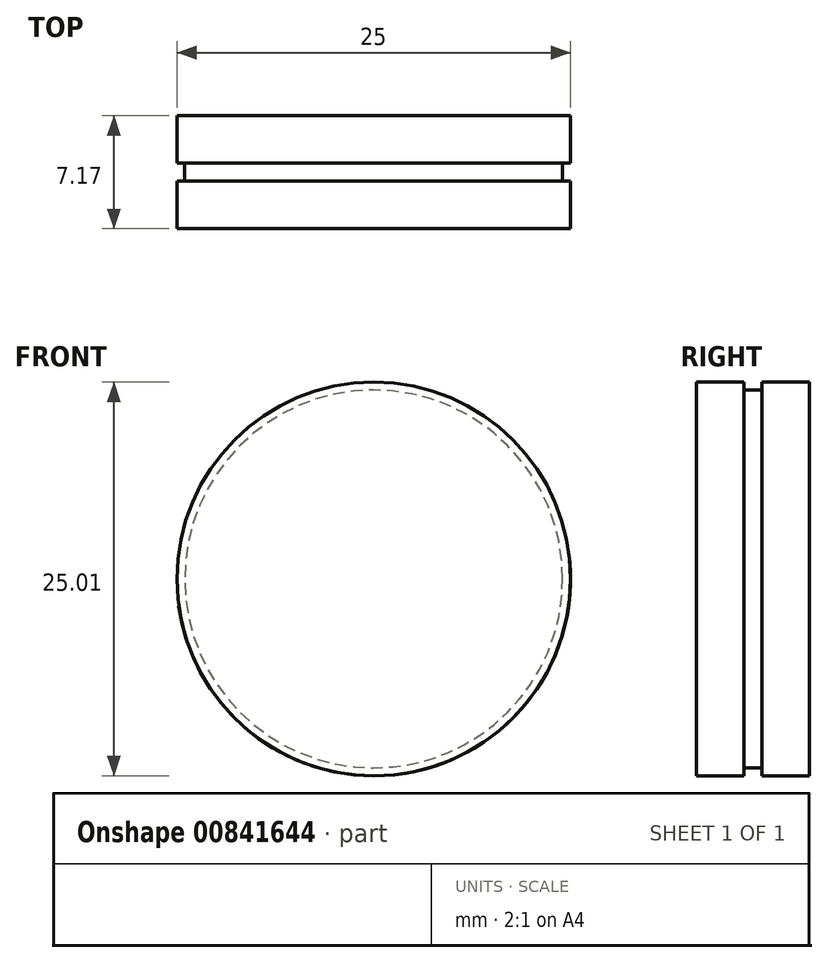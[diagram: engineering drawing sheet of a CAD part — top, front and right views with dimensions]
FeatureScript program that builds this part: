
annotation { "Feature Type Name" : "Feature", "Feature Type Description" : "" }
export const myFeature = defineFeature(function(context is Context, id is Id, definition is map)
    precondition{}
    {
        {
            var Q0;
            Q0=qCreatedBy(makeId("Front.planeOp"),FACE);
            var sketch = newSketch(context, id + "F0", { "sketchPlane" : qUnion([Q0])});
            skCircle(sketch, "E0", {"center": v(-49, 23.24) * mm, "radius": 12.5 * mm});
            skSolve(sketch);
        }
        {
            var Q0;
            Q0 = qSketchRegion(id + "F0", true);
            extrude(context, id + "F1", {"entities" : qUnion([Q0]), "depth" : 3 * mm, "offsetDistance" : 25 * mm});
        }
        {
            var Q0;
            Q0=makeQuery(id+"F1.opExtrude","CAP_FACE",FACE,{"disambiguationData":[OSD([sQuery(id+"F0.wireOp",EDGE,"E0")])],"isStart":false});
            var sketch = newSketch(context, id + "F2", { "sketchPlane" : qUnion([Q0])});
            skCircle(sketch, "E1", {"center": v(-49, 23.25) * mm, "radius": 12 * mm});
            skSolve(sketch);
        }
        {
            var Q0;
            Q0=makeQuery(id+"F2.imprint","IMPRINT",FACE,{"disambiguationData":[TD([[makeQuery(id+"F2.imprint","IMPRINT",EDGE,{"derivedFrom":sQuery(id+"F2.wireOp",EDGE,"E1")}),1.0]])]});
            extrude(context, id + "F3", {"entities" : qUnion([Q0]), "operationType" : NewBodyOperationType.ADD, "depth" : 1.67 * mm, "offsetDistance" : 25 * mm});
        }
        {
            var Q0;
            Q0=makeQuery(id+"F3.opExtrude","CAP_FACE",FACE,{"disambiguationData":[OSD([sQuery(id+"F2.wireOp",EDGE,"E1")])],"isStart":false});
            var sketch = newSketch(context, id + "F4", { "sketchPlane" : qUnion([Q0])});
            skCircle(sketch, "E2", {"center": v(-49, 23.25) * mm, "radius": 12.5 * mm});
            skSolve(sketch);
        }
        {
            var Q0;
            Q0=makeQuery(id+"F4.imprint","IMPRINT",FACE,{"disambiguationData":[TD([[makeQuery(id+"F4.imprint","IMPRINT",EDGE,{"derivedFrom":sQuery(id+"F4.wireOp",EDGE,"E2")}),1.0]])]});
            var Q1;
            Q1=makeQuery(id+"F4.imprint","IMPRINT",FACE,{"disambiguationData":[TD([[makeQuery(id+"F4.imprint","IMPRINT",EDGE,{"derivedFrom":makeQuery(id+"F3.opExtrude","CAP_EDGE",EDGE,{"disambiguationData":[OSD([sQuery(id+"F2.wireOp",EDGE,"E1")])],"isStart":false})}),1.0]])]});
            extrude(context, id + "F5", {"entities" : qUnion([Q0, Q1]), "operationType" : NewBodyOperationType.ADD, "depth" : 2.5 * mm, "offsetDistance" : 25 * mm, "hasSecondDirection" : true, "secondDirectionOppositeDirection" : true, "secondDirectionDepth" : 0.5 * mm});
        }
    });
